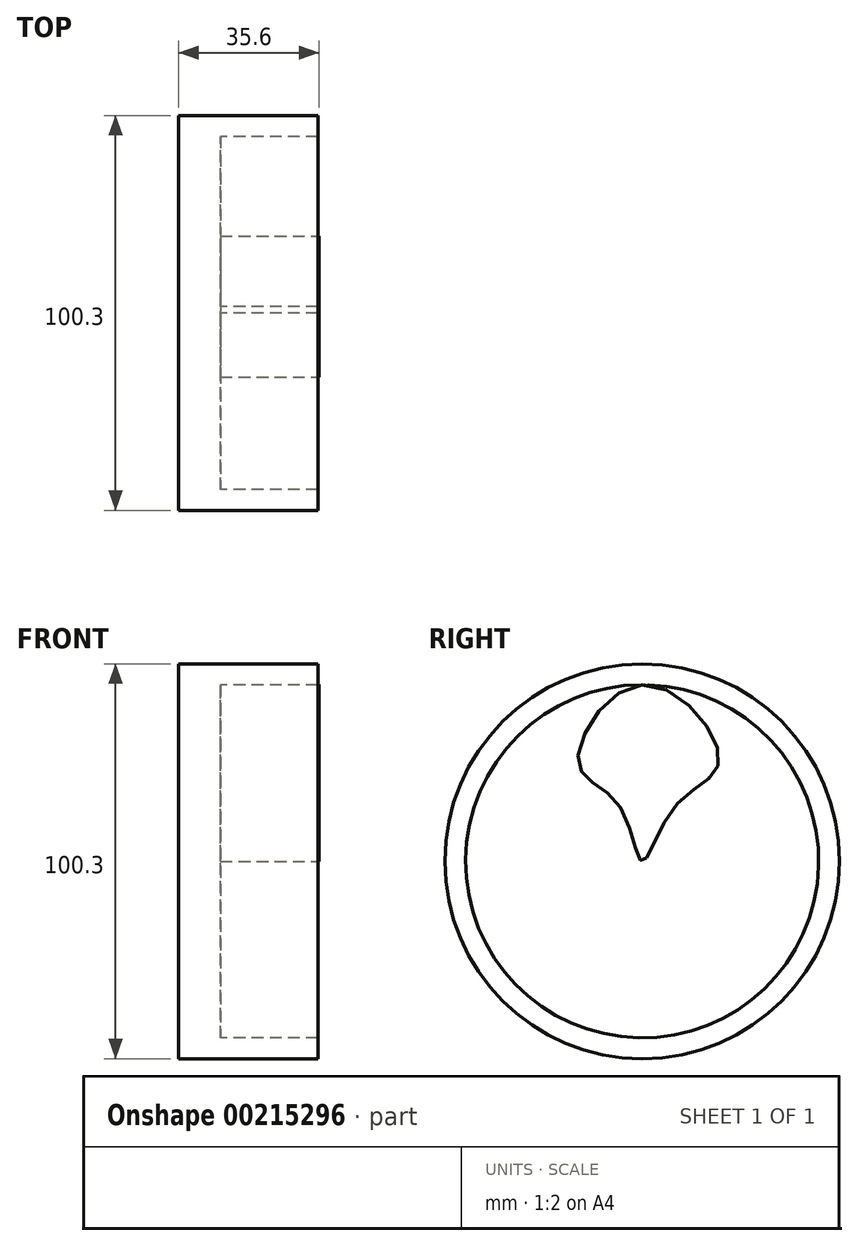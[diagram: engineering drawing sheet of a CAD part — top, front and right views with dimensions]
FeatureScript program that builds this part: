
annotation { "Feature Type Name" : "Feature", "Feature Type Description" : "" }
export const myFeature = defineFeature(function(context is Context, id is Id, definition is map)
    precondition{}
    {
        {
            var Q0;
            Q0=qCreatedBy(makeId("Front.planeOp"),FACE);
            var sketch = newSketch(context, id + "F0", { "sketchPlane" : qUnion([Q0])});
            skLineSegment(sketch, "E0", {"start": v(0, 0) * mm, "end": v(0, 50.15) * mm});
            skLineSegment(sketch, "E1", {"start": v(0, 50.15) * mm, "end": v(35.35, 50.15) * mm});
            skLineSegment(sketch, "E2", {"start": v(35.35, 50.15) * mm, "end": v(35.35, 44.85) * mm});
            skLineSegment(sketch, "E3", {"start": v(35.35, 44.85) * mm, "end": v(10.6, 44.85) * mm});
            skLineSegment(sketch, "E4", {"start": v(10.6, 44.85) * mm, "end": v(10.6, 0) * mm});
            skLineSegment(sketch, "E5", {"start": v(10.6, 0) * mm, "end": v(0, 0) * mm});
            skLineSegment(sketch, "E6", {"start": v(-74.23, 0) * mm, "end": v(74.23, 0) * mm, "construction": true});
            skSolve(sketch);
        }
        {
            var Q0;
            Q0=makeQuery(id+"F0.imprint","IMPRINT",FACE,{"disambiguationData":[TD([[makeQuery(id+"F0.imprint","IMPRINT",EDGE,{"derivedFrom":sQuery(id+"F0.wireOp",EDGE,"E0")}),-1.0]])]});
            var Q1;
            Q1=sQuery(id+"F0.wireOp",EDGE,"E6");
            revolve(context, id + "F1", {"entities" : qUnion([Q0]), "axis" : qUnion([Q1]), "revolveType" : RevolveType.FULL});
        }
        {
            var Q0;
            Q0=makeQuery(id+"F1.opRevolve","SWEPT_FACE",FACE,{"disambiguationData":[OSD([sQuery(id+"F0.wireOp",EDGE,"E4")])]});
            var sketch = newSketch(context, id + "F2", { "sketchPlane" : qUnion([Q0])});
            skFitSpline(sketch, "E7", {"points": [v(0, 44.85) * mm, v(-16.2, 24.76) * mm, v(-6, 14.46) * mm, v(0, 0) * mm, v(8.5, 14.1) * mm, v(19.58, 25.92) * mm, v(0, 44.85) * mm]});
            skSolve(sketch);
        }
        {
            var Q0;
            Q0 = qSketchRegion(id + "F2", true);
            extrude(context, id + "F3", {"entities" : qUnion([Q0]), "operationType" : NewBodyOperationType.ADD, "depth" : 25 * mm});
        }
    });
